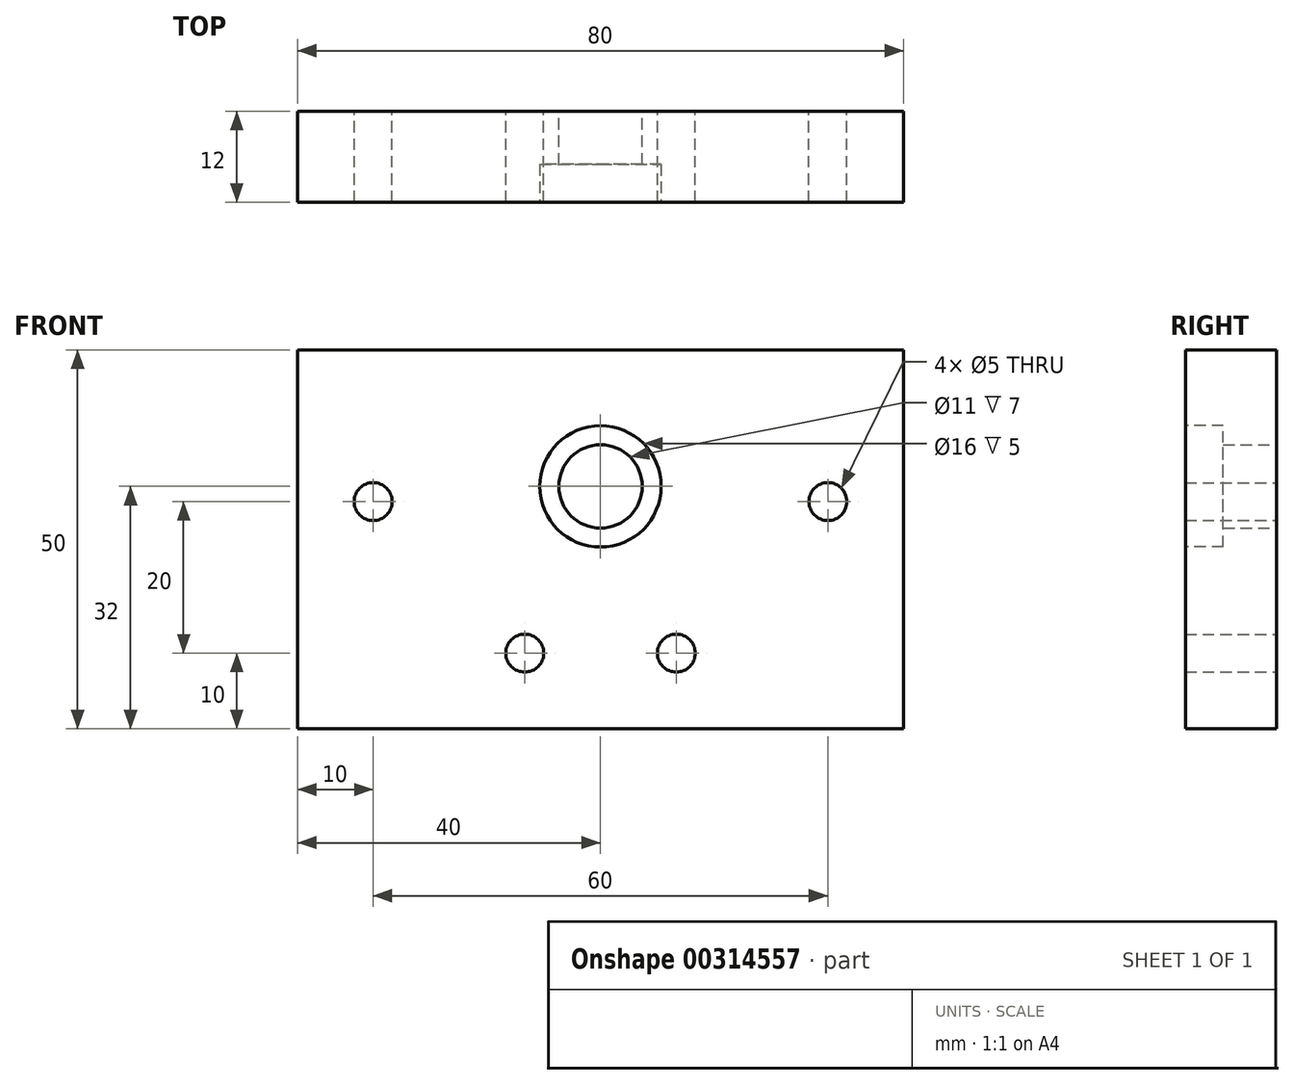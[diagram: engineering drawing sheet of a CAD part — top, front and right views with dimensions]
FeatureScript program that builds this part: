
annotation { "Feature Type Name" : "Feature", "Feature Type Description" : "" }
export const myFeature = defineFeature(function(context is Context, id is Id, definition is map)
    precondition{}
    {
        {
            var Q0;
            Q0=qCreatedBy(makeId("Front.planeOp"),FACE);
            var sketch = newSketch(context, id + "F0", { "sketchPlane" : qUnion([Q0])});
            skLineSegment(sketch, "E0.bottom", {"start": v(-40, 25) * mm, "end": v(40, 25) * mm});
            skLineSegment(sketch, "E0.top", {"start": v(-40, -25) * mm, "end": v(40, -25) * mm});
            skLineSegment(sketch, "E0.left", {"start": v(-40, 25) * mm, "end": v(-40, -25) * mm});
            skLineSegment(sketch, "E0.right", {"start": v(40, 25) * mm, "end": v(40, -25) * mm});
            skPoint(sketch, "E0.middle", {"position": v(0, 0) * mm});
            skPoint(sketch, "E1", {"position": v(-30, 5) * mm});
            skPoint(sketch, "E2.MirrorP", {"position": v(30, 5) * mm});
            skPoint(sketch, "E3", {"position": v(-10, -15) * mm});
            skPoint(sketch, "E4.MirrorP", {"position": v(10, -15) * mm});
            skCircle(sketch, "E5", {"center": v(-30, 5) * mm, "radius": 2.5 * mm});
            skCircle(sketch, "E6", {"center": v(-10, -15) * mm, "radius": 2.5 * mm});
            skCircle(sketch, "E7.MirrorC", {"center": v(30, 5) * mm, "radius": 2.5 * mm});
            skCircle(sketch, "E8.MirrorC", {"center": v(10, -15) * mm, "radius": 2.5 * mm});
            skCircle(sketch, "E9", {"center": v(0, 7) * mm, "radius": 5.5 * mm});
            skSolve(sketch);
        }
        {
            var Q0;
            Q0 = qSketchRegion(id + "F0", true);
            extrude(context, id + "F1", {"entities" : qUnion([Q0]), "depth" : 12 * mm});
        }
        {
            var Q0;
            Q0=makeQuery(id+"F1.opExtrude","CAP_FACE",FACE,{"disambiguationData":[OSD([sQuery(id+"F0.wireOp",EDGE,"E0.bottom"),sQuery(id+"F0.wireOp",EDGE,"E0.top"),sQuery(id+"F0.wireOp",EDGE,"E0.left"),sQuery(id+"F0.wireOp",EDGE,"E0.right"),sQuery(id+"F0.wireOp",EDGE,"E5"),sQuery(id+"F0.wireOp",EDGE,"E6"),sQuery(id+"F0.wireOp",EDGE,"E7.MirrorC"),sQuery(id+"F0.wireOp",EDGE,"E8.MirrorC"),sQuery(id+"F0.wireOp",EDGE,"E9")])],"isStart":false});
            var sketch = newSketch(context, id + "F2", { "sketchPlane" : qUnion([Q0])});
            skCircle(sketch, "E10", {"center": v(0, 7) * mm, "radius": 8 * mm});
            skSolve(sketch);
        }
        {
            var Q0;
            Q0=makeQuery(id+"F2.imprint","IMPRINT",FACE,{"disambiguationData":[TD([[makeQuery(id+"F2.imprint","IMPRINT",EDGE,{"derivedFrom":sQuery(id+"F2.wireOp",EDGE,"E10")}),1.0]])]});
            extrude(context, id + "F3", {"entities" : qUnion([Q0]), "operationType" : NewBodyOperationType.REMOVE, "oppositeDirection" : true, "depth" : 5 * mm});
        }
    });
